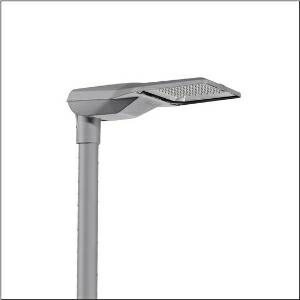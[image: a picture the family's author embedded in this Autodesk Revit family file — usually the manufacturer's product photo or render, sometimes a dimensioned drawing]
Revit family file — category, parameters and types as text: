
# Revit family: streetlight_sl_21_midi___st0_8a_5xe7c43a08lb_78a7
name_source: partatom
category: Lighting Fixtures
units: mm (PartAtom-declared; Revit-internal decimal feet)

## family parameters
Cut with Voids When Loaded = No
Host = Face
Light Source = No
Part Type = Normal
Room Calculation Point = No
Round Connector Dimension = Use Diameter
Shared = No

## types (1)
- --- (1 x LED, 14950 lm, 98.3 W, 4000K)
    Apparent Load = 98 VA
    CIE Flux Codes = 38 75 97 100 100
    Color Rendering = 70
    Color Temperature = 4000K
    Default Elevation = 1800 mm
    Description = Streetlight SL 21 midi, mast luminaire, primary light control with lens, of PMMA, primary optical cover: cover, of toughened safety glass, transparent, light distribution: ST0.8a, light emission: direct distribution, primary light characteristic: asymmetric, installation type: post-top, side-entry, LED, 3G 1.5mm², High Power LED, rated luminous flux: 14.950lm, luminous efficacy: 152lm/W, light colour: 740, colour temperature: 4000K, control gear: Easy, control: overheat protection, constant luminous flux control, time-dependent luminous flux control, flexible luminous flux parameterisation, mains connection: 220..240V, AC, 50/60Hz, connection cable pre-assembled, cable length: 10,5m, wiring characteristics: H07RN-F, start of lifetime: 98W, end of service life: 101W, reduction: 45W, luminaire housing, of diecast aluminium, powder-coated, Siteco® metallic grey (DB 702S), corrosivity category C5 mid according to DIN EN ISO 12944, please order mast flange separately, inclination adjustable: 0°, 5°, 10°, 15°, sealing non-destructively replaceable, multi-level sealing system, length: 644mm, width: 335mm, height: 110mm, mast flange for spigot size: 42mm (side-entry): 5XC10008XM4, 60/48mm (side-entry/post-top): 5XC10108XM2, 76/60mm (side-entry/post-top): 5XC10108XM1, mounting height: 4..8m, protection rating (complete): IP66, insulation class (complete): insulation class II (safety insulation), certification: CE, ENEC, ENEC+, VDE, impact resistance: IK10, permissible operating ambient temperature for outdoor applications: -40..+50°C, standard-compliant lighting for roads and squares, packaging unit: 1 piece

Light Distribution: ST0.8a
    Height = 111 mm
    Lamp = 1 x LED
    Lamp Light Flux = 14950 lm
    Lamp Power = 98.3 W
    Lamp count = 1
    Length = 644 mm
    Luminous efficacy = 152 lm/W
    Manufacturer = Siteco
    ModVariant = No
    Model = 5XE7C43A08LB
    Number of Poles = 1
    OnlyDefault = Yes
    Power Factor = 1
    Product Name = Streetlight SL 21 midi | ST0.8a
    Product group = mast luminaire | pylon top
    ProductGroupID = 6100
    Protection Class = Protection class II
    Protection Degree = IP 66
    RLX_Detail_Level = 1
    RLX_Emergency_Light_Flux = 0 lm
    RLX_Emergency_Type = 0
    RLX_Emergency_Type_DB = No
    RlxData = <blob elided: 26933 chars, md5=d78c227e>
    Socket = socket
    Standby Power = 0 W
    System Light Flux = 14950 lm
    System Power = 98 W
    Type Comments = factory setting: luminous flux: 100 % | Output Level: 100 % | 1020 mA
    Type Image = l_1004298.jpg
    URL = http://relux.com
    VarID = @adj_207171
    Voltage = 0 V
    Weight = 0.00 kg
    Width = 336 mm

## geometry (parser evidence)
native form markers: Blend x4, Sweep x10
no freeform markers — native parametric forms only
